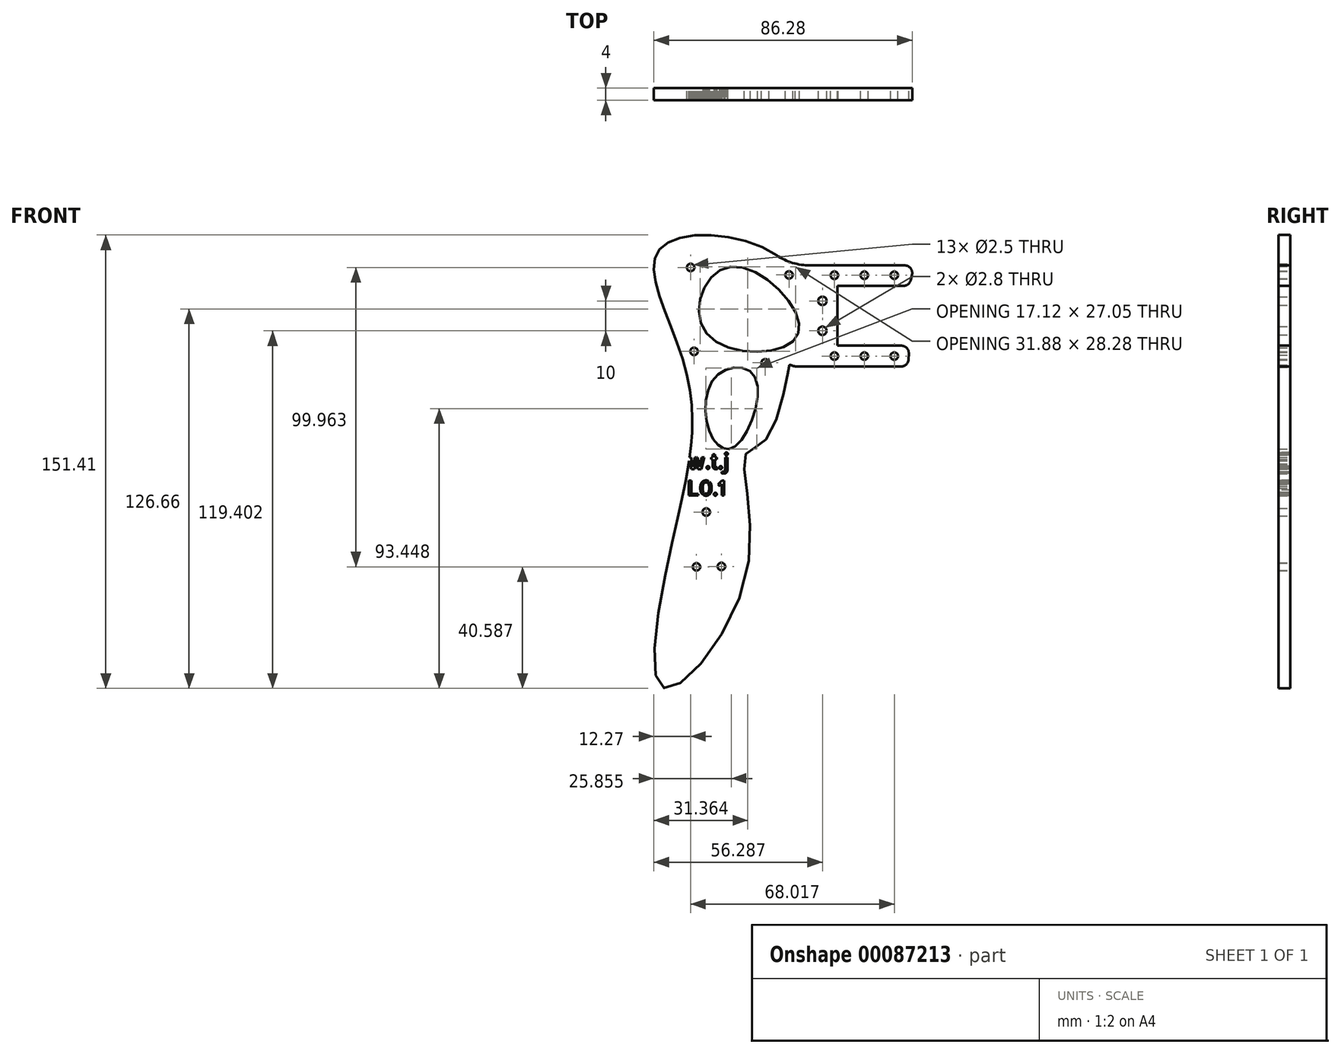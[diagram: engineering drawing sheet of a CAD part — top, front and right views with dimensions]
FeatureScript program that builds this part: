
annotation { "Feature Type Name" : "Feature", "Feature Type Description" : "" }
export const myFeature = defineFeature(function(context is Context, id is Id, definition is map)
    precondition{}
    {
        {
            var Q0;
            Q0=qCreatedBy(makeId("Front.planeOp"),FACE);
            var sketch = newSketch(context, id + "F0", { "sketchPlane" : qUnion([Q0])});
            skLineSegment(sketch, "E0", {"start": v(37.5, 6.99) * mm, "end": v(16.15, 6.99) * mm});
            skLineSegment(sketch, "E1", {"start": v(16.15, 6.99) * mm, "end": v(16.15, 26.99) * mm});
            skLineSegment(sketch, "E2", {"start": v(16.15, 26.99) * mm, "end": v(38.28, 26.99) * mm});
            skLineSegment(sketch, "E3", {"start": v(38.64, 33.78) * mm, "end": v(7.01, 33.78) * mm});
            skLineSegment(sketch, "E4", {"start": v(2.09, 0) * mm, "end": v(37.38, 0) * mm});
            skLineSegment(sketch, "E5", {"start": v(41.07, 30.69) * mm, "end": v(40.6, 28.81) * mm});
            skLineSegment(sketch, "E6", {"start": v(40, 4.34) * mm, "end": v(39.87, 2.35) * mm});
            skCircle(sketch, "E7", {"center": v(35.15, 30.5) * mm, "radius": 1.25 * mm});
            skCircle(sketch, "E8", {"center": v(25.15, 30.5) * mm, "radius": 1.25 * mm});
            skCircle(sketch, "E9", {"center": v(15.15, 30.5) * mm, "radius": 1.25 * mm});
            skCircle(sketch, "E10", {"center": v(15.15, 3.5) * mm, "radius": 1.25 * mm});
            skCircle(sketch, "E11", {"center": v(35.15, 3.5) * mm, "radius": 1.25 * mm});
            skCircle(sketch, "E12", {"center": v(25.15, 3.5) * mm, "radius": 1.25 * mm});
            skPoint(sketch, "E13.start.orphan", {"position": v(41, 30.39) * mm});
            skPoint(sketch, "E14.trimOffspring.end.orphan", {"position": v(2.12, 0) * mm});
            skPoint(sketch, "E15.trimOffspring.end.orphan", {"position": v(25.15, 0) * mm});
            skPoint(sketch, "E16.trimOffspring.end.orphan", {"position": v(35.15, 0) * mm});
            skPoint(sketch, "E17", {"position": v(-43.02, 39.43) * mm});
            skPoint(sketch, "E18", {"position": v(-34.78, 0) * mm});
            skPoint(sketch, "E19", {"position": v(-7.63, -24.34) * mm});
            skPoint(sketch, "E20", {"position": v(-14.4, -70.1) * mm});
            skPoint(sketch, "E21", {"position": v(-14.4, -29.13) * mm});
            skPoint(sketch, "E22", {"position": v(-34.13, -36.16) * mm});
            skPoint(sketch, "E23", {"position": v(-39.22, -59.46) * mm});
            skPoint(sketch, "E24", {"position": v(-42.36, -107.08) * mm});
            skFitSpline(sketch, "E25", {"points": [v(0, 33.78) * mm, v(-43.02, 39.43) * mm, v(-34.78, 0) * mm, v(-34.13, -36.16) * mm, v(-39.22, -59.46) * mm, v(-42.36, -107.08) * mm, v(-14.4, -70.1) * mm, v(-14.4, -29.13) * mm, v(-7.63, -24.34) * mm, v(0, 0) * mm, v(2.12, 0) * mm], "startDerivative": vector(-258.8, 266.92) * mm, "endDerivative": vector(218.15, -65.47) * mm});
            skPoint(sketch, "E26", {"position": v(-37.41, -106.34) * mm});
            skPoint(sketch, "E27", {"position": v(-19.5, 33.34) * mm});
            skPoint(sketch, "E28", {"position": v(-27.6, 11.13) * mm});
            skPoint(sketch, "E29", {"position": v(3.02, 10.83) * mm});
            skPoint(sketch, "E30", {"position": v(-11.64, -3.09) * mm});
            skPoint(sketch, "E31", {"position": v(-24.69, -3.49) * mm});
            skPoint(sketch, "E32", {"position": v(-25.36, -24.18) * mm});
            skPoint(sketch, "E33", {"position": v(-17.8, -26.48) * mm});
            skFitSpline(sketch, "E34", {"points": [v(-25.36, -24.18) * mm, v(-24.69, -3.49) * mm, v(-11.64, -3.09) * mm, v(-17.8, -26.48) * mm, v(-25.36, -24.18) * mm]});
            skFitSpline(sketch, "E35", {"points": [v(-19.5, 33.34) * mm, v(-27.6, 11.13) * mm, v(3.02, 10.83) * mm, v(-19.5, 33.34) * mm]});
            skPoint(sketch, "E36", {"position": v(-29.96, 16.68) * mm});
            skPoint(sketch, "E37", {"position": v(-26.06, 29.68) * mm});
            skPoint(sketch, "E38", {"position": v(-27.89, -14.25) * mm});
            skArc(sketch, "E39.filletArc", {"start": v(-4.09, 37.15) * mm, "mid": v(1.21, 34.64) * mm, "end": v(7.01, 33.78) * mm});
            skCircle(sketch, "E40", {"center": v(-32.87, 33.09) * mm, "radius": 1.25 * mm});
            skCircle(sketch, "E41", {"center": v(0, 30.61) * mm, "radius": 1.25 * mm});
            skCircle(sketch, "E42", {"center": v(-31.72, 5.06) * mm, "radius": 1.25 * mm});
            skCircle(sketch, "E43", {"center": v(-7.96, 1.25) * mm, "radius": 1.25 * mm});
            skCircle(sketch, "E44", {"center": v(-22.59, -66.73) * mm, "radius": 1.25 * mm});
            skPoint(sketch, "E45.visualSharp", {"position": v(41.83, 33.78) * mm});
            skArc(sketch, "E45.filletArc", {"start": v(41.07, 30.69) * mm, "mid": v(40.6, 32.83) * mm, "end": v(38.64, 33.78) * mm});
            skPoint(sketch, "E46.visualSharp", {"position": v(40.16, 26.99) * mm});
            skArc(sketch, "E46.filletArc", {"start": v(38.28, 26.99) * mm, "mid": v(39.76, 27.5) * mm, "end": v(40.6, 28.81) * mm});
            skPoint(sketch, "E47.visualSharp", {"position": v(40.15, 6.99) * mm});
            skArc(sketch, "E47.filletArc", {"start": v(40, 4.34) * mm, "mid": v(39.32, 6.2) * mm, "end": v(37.5, 6.99) * mm});
            skPoint(sketch, "E48.visualSharp", {"position": v(39.73, 0) * mm});
            skArc(sketch, "E48.filletArc", {"start": v(37.38, 0) * mm, "mid": v(39.1, 0.68) * mm, "end": v(39.87, 2.35) * mm});
            skArc(sketch, "E49.filletArc", {"start": v(2.09, 0) * mm, "mid": v(0.49, -0.58) * mm, "end": v(-0.37, -2.05) * mm});
            skCircle(sketch, "E50", {"center": v(-30.93, -66.87) * mm, "radius": 1.25 * mm});
            skPoint(sketch, "E51.endSnap0", {"position": v(16.15, 16.99) * mm});
            skCircle(sketch, "E52", {"center": v(11.15, 21.94) * mm, "radius": 1.4 * mm});
            skCircle(sketch, "E53", {"center": v(11.15, 11.94) * mm, "radius": 1.4 * mm});
            skCircle(sketch, "E54", {"center": v(-27.65, -48.57) * mm, "radius": 1.25 * mm});
            skText(sketch, "E55", { "text": "w.t.j\nL0.1", "fontName": "AllertaStencil-Regular.ttf"});
            skPoint(sketch, "E56", {"position": v(-4.34, -17.84) * mm});
            const initialGuessF0  = {"E55": [-0.03412, -0.03418, 1, 0, 0.005]};
            skSetInitialGuess(sketch, initialGuessF0);
            skSolve(sketch);
        }
        {
            var Q0;
            Q0=makeQuery(id+"F0.imprint","IMPRINT",FACE,{"disambiguationData":[TD([[makeQuery(id+"F0.imprint","IMPRINT",EDGE,{"derivedFrom":sQuery(id+"F0.wireOp",EDGE,"E0")}),1.0]])]});
            extrude(context, id + "F1", {"entities" : qUnion([Q0]), "depth" : 4 * mm});
        }
    });
